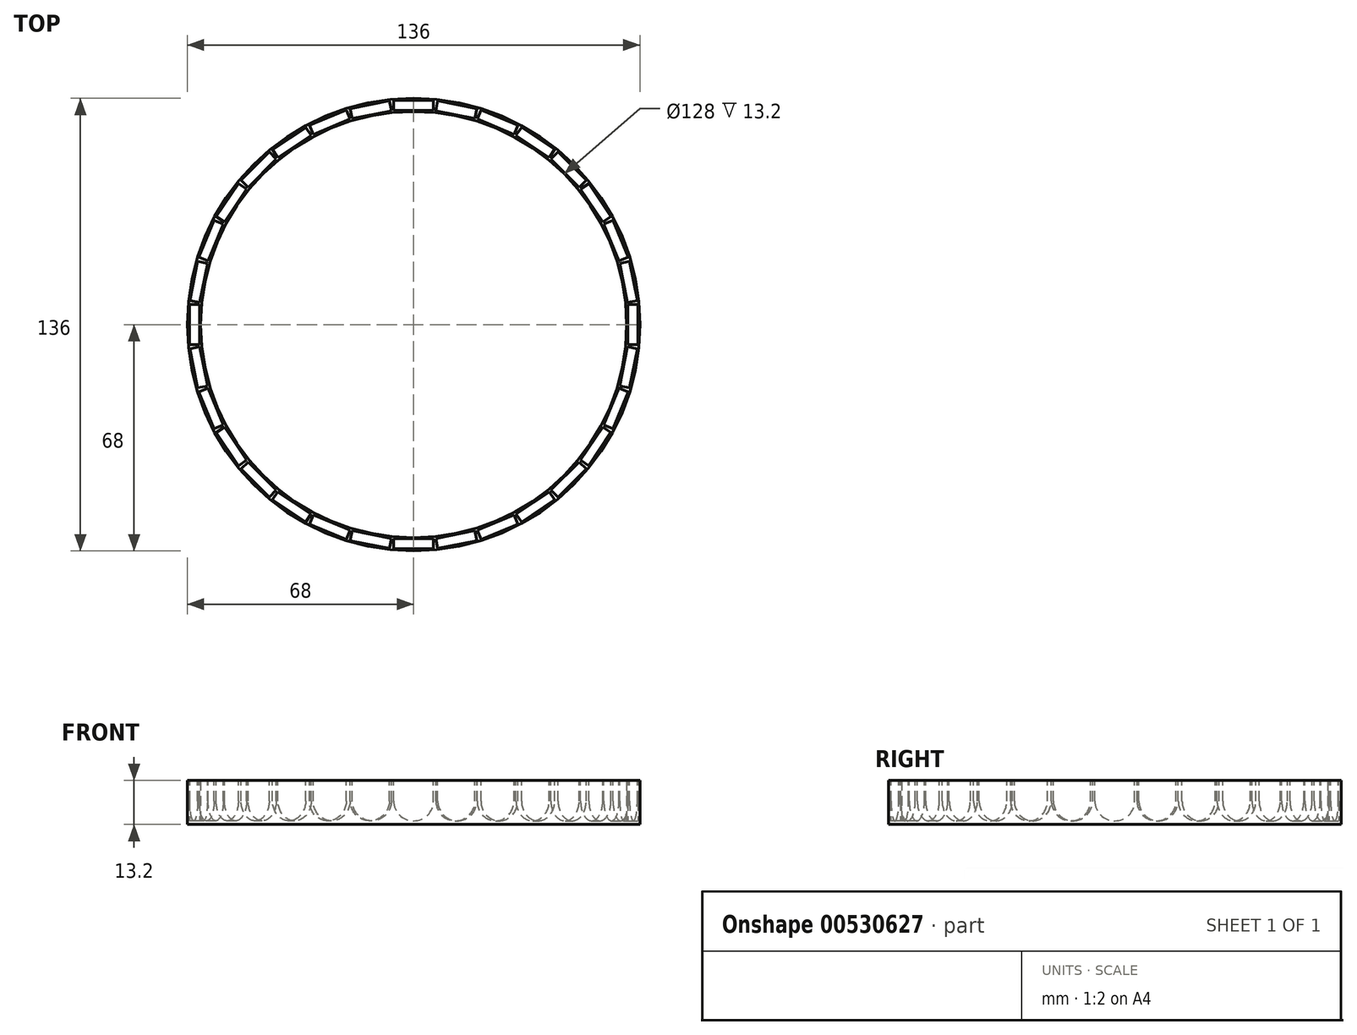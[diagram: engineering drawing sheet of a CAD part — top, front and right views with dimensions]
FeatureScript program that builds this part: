
annotation { "Feature Type Name" : "Feature", "Feature Type Description" : "" }
export const myFeature = defineFeature(function(context is Context, id is Id, definition is map)
    precondition{}
    {
        {
            var Q0;
            Q0=qCreatedBy(makeId("Front.planeOp"),FACE);
            var sketch = newSketch(context, id + "F0", { "sketchPlane" : qUnion([Q0])});
            skPoint(sketch, "E0", {"position": v(-66, 0) * mm});
            skPoint(sketch, "E1", {"position": v(-66, 18.49) * mm});
            skLineSegment(sketch, "E2", {"start": v(-66, 18.49) * mm, "end": v(-68, 18.49) * mm});
            skLineSegment(sketch, "E3", {"start": v(-66, 18.49) * mm, "end": v(-64, 18.49) * mm});
            skLineSegment(sketch, "E4", {"start": v(-68, 18.49) * mm, "end": v(-68, 31.69) * mm});
            skLineSegment(sketch, "E5", {"start": v(-68, 31.69) * mm, "end": v(-64, 31.69) * mm});
            skLineSegment(sketch, "E6", {"start": v(-64, 31.69) * mm, "end": v(-64, 18.49) * mm});
            skLineSegment(sketch, "E7", {"start": v(0, 0) * mm, "end": v(0, 20.09) * mm});
            skSolve(sketch);
        }
        {
            var Q0;
            Q0 = qSketchRegion(id + "F0", true);
            var Q1;
            Q1=sQuery(id+"F0.wireOp",EDGE,"E7");
            revolve(context, id + "F1", {"entities" : qUnion([Q0]), "axis" : qUnion([Q1]), "revolveType" : RevolveType.FULL});
        }
        {
            var Q0;
            Q0=qCreatedBy(makeId("Front.planeOp"),FACE);
            cPlane(context, id + "F2", {"entities" : qUnion([Q0]), "cplaneType" : CPlaneType.OFFSET, "offset" : 65.85 * mm, "width" : 150 * mm, "height" : 150 * mm});
        }
        {
            var Q0;
            Q0=qCreatedBy(id+"F2.planeOp",FACE);
            var sketch = newSketch(context, id + "F3", { "sketchPlane" : qUnion([Q0])});
            skCircle(sketch, "E8", {"center": v(0, 25.59) * mm, "radius": 6 * mm});
            skLineSegment(sketch, "E9", {"start": v(-6, 25.59) * mm, "end": v(-6, 37.05) * mm});
            skLineSegment(sketch, "E10", {"start": v(6, 25.59) * mm, "end": v(6, 37.05) * mm});
            skLineSegment(sketch, "E11", {"start": v(6, 37.05) * mm, "end": v(-6, 37.05) * mm});
            skSolve(sketch);
        }
        {
            var Q0;
            Q0 = qSketchRegion(id + "F3", true);
            extrude(context, id + "F4", {"entities" : qUnion([Q0]), "oppositeDirection" : true, "depth" : 1.5 * mm, "offsetDistance" : 25 * mm, "hasSecondDirection" : true, "secondDirectionOppositeDirection" : false, "secondDirectionDepth" : 1.5 * mm});
        }
        {
            var Q0;
            Q0=makeQuery(id+"F4.opExtrude","SWEPT_BODY",BODY,{"disambiguationData":[OSD([sQuery(id+"F3.wireOp",EDGE,"E8"),sQuery(id+"F3.wireOp",EDGE,"E9"),sQuery(id+"F3.wireOp",EDGE,"E10"),sQuery(id+"F3.wireOp",EDGE,"E11")])]});
            var Q1;
            Q1=sQuery(id+"F0.wireOp",EDGE,"E7");
            circularPattern(context, id + "F5", {"operationType" : NewBodyOperationType.REMOVE, "entities" : qUnion([Q0]), "axis" : qUnion([Q1]), "angle" : 360 * degree, "instanceCount" : 32, "equalSpace" : true});
        }
    });
